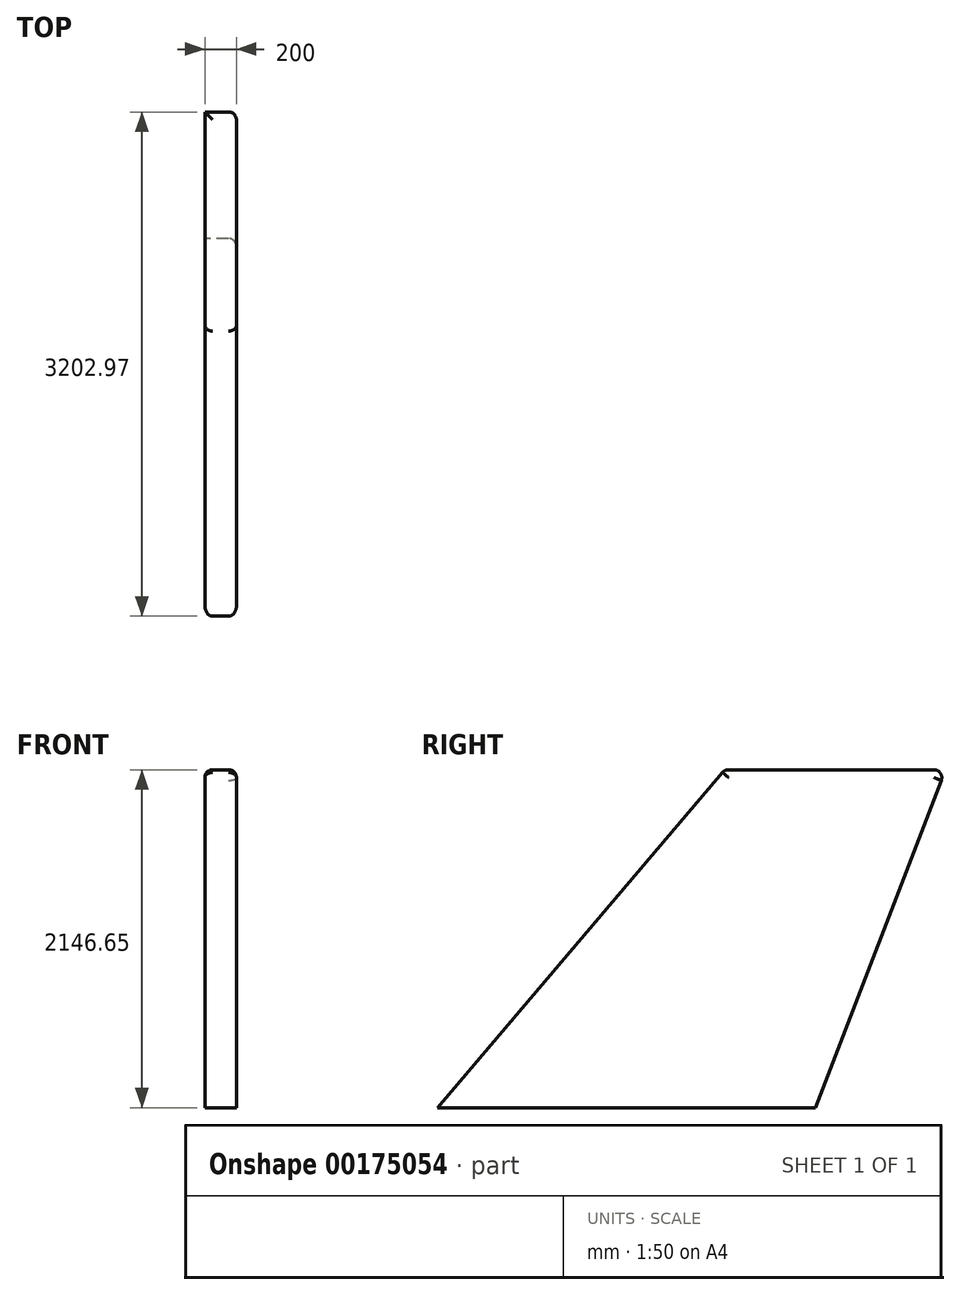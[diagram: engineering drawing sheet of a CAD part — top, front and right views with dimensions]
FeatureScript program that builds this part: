
annotation { "Feature Type Name" : "Feature", "Feature Type Description" : "" }
export const myFeature = defineFeature(function(context is Context, id is Id, definition is map)
    precondition{}
    {
        {
            var Q0;
            Q0=qCreatedBy(makeId("Right.planeOp"),FACE);
            var sketch = newSketch(context, id + "F0", { "sketchPlane" : qUnion([Q0])});
            skLineSegment(sketch, "E0", {"start": v(-1318.74, 0) * mm, "end": v(1081.26, 0) * mm});
            skLineSegment(sketch, "E1", {"start": v(1081.26, 0) * mm, "end": v(1907.04, 2146.65) * mm});
            skLineSegment(sketch, "E2", {"start": v(1907.04, 2146.65) * mm, "end": v(507.04, 2146.65) * mm});
            skLineSegment(sketch, "E3", {"start": v(507.04, 2146.65) * mm, "end": v(-1318.74, 0) * mm});
            skSolve(sketch);
        }
        {
            var Q0;
            Q0=qCreatedBy(makeId("Front.planeOp"),FACE);
            var sketch = newSketch(context, id + "F1", { "sketchPlane" : qUnion([Q0])});
            skSolve(sketch);
        }
        {
            var Q0;
            Q0=qSketchRegion(id+"F1",true);
            var Q1;
            Q1=makeQuery(id+"F0.imprint","IMPRINT",FACE,{"disambiguationData":[TD([[makeQuery(id+"F0.imprint","IMPRINT",EDGE,{"derivedFrom":sQuery(id+"F0.wireOp",EDGE,"E0")}),1.0]])]});
            extrude(context, id + "F2", {"entities" : qUnion([Q0, Q1]), "endBound" : BoundingType.SYMMETRIC, "depth" : 200 * mm});
        }
        {
            var Q0;
            Q0=makeQuery(id+"F2.opExtrude","CAP_EDGE",EDGE,{"disambiguationData":[OSD([sQuery(id+"F0.wireOp",EDGE,"E3")])],"isStart":true});
            var Q1;
            Q1=makeQuery(id+"F2.opExtrude","CAP_EDGE",EDGE,{"disambiguationData":[OSD([sQuery(id+"F0.wireOp",EDGE,"E3")])],"isStart":false});
            var Q2;
            Q2=makeQuery(id+"F2.opExtrude","CAP_EDGE",EDGE,{"disambiguationData":[OSD([sQuery(id+"F0.wireOp",EDGE,"E1")])],"isStart":false});
            fillet(context, id + "F3", {"entities" : qUnion([Q0, Q1, Q2]), "radius" : 50 * mm, "tangentPropagation" : true, "allowEdgeOverflow" : false});
        }
        {
            var Q0;
            Q0=makeQuery(id+"F2.opExtrude","CAP_EDGE",EDGE,{"disambiguationData":[OSD([sQuery(id+"F0.wireOp",EDGE,"E2")])],"isStart":false});
            var Q1;
            Q1=makeQuery(id+"F2.opExtrude","CAP_EDGE",EDGE,{"disambiguationData":[OSD([sQuery(id+"F0.wireOp",EDGE,"E2")])],"isStart":true});
            fillet(context, id + "F4", {"entities" : qUnion([Q0, Q1]), "radius" : 50 * mm, "tangentPropagation" : true, "allowEdgeOverflow" : false});
        }
    });
